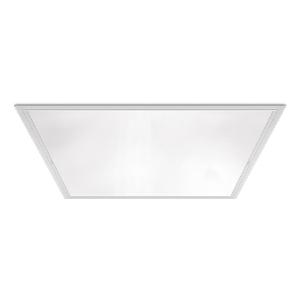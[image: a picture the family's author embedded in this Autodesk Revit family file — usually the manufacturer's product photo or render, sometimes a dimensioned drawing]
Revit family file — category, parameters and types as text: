
# Revit family: 3f_filippi_-_l_340_luce_diffusa_lgs_ip65v_3f_filippi_-_23979_-_l_340_38w-840_dali_lgs_ip65v_596x596
name_source: partatom
category: Lighting Fixtures
units: mm (PartAtom-declared; Revit-internal decimal feet)

## family parameters
Cut with Voids When Loaded = No
Host = Face
Light Source = No
Part Type = Normal
Room Calculation Point = No
Round Connector Dimension = Use Diameter
Shared = No

## types (1)
- 3F Filippi - L 340 Luce Diffusa LGS IP65V (1 x LED, 5677 lm, 43 W, 4000 K)
    Apparent Load = 43 VA
    Approval mark = ENEC
    CIE Flux Codes = 67 92 98 100 100
    Color Rendering = 80
    Color Temperature = 4000 K
    Control Gear = Electronic transformer
    Default Elevation = 1800 mm
    Description = ILLUMINOTECHNICAL
Luminous efficiency 100% (DLOR 100%, ULOR 0%).
Initial luminous flux of the luminaire 5677 lm.
Direct symmetric distribution.
Installation Interdistance Transv.D = 1.19 x hu - Long.D = 1.17 x hu.
Average luminance <3000 cd/m² for radial angles >65°.
Tabular UGR (CIE 117 - 4H-8H; S=0.25H; 70/50/20): RUG 17.8 - 17.8.
Beam angle: 87° - 86°.
Luminous efficacy 132 lm/W.
Lifetime (L93/B10): 30000 h. (tq+25°C)
Lifetime (L90/B10): 50000 h. (tq+25°C)
Lifetime (L85/B10): 80000 h. (tq+25°C)
Lifetime (L80/B10): 100000 h. (tq+25°C)
Sudden decreased luminous flux after 50000 hours: 0% (C0).
Photobiological safety in compliance with IEC/TR 62778: RG0 risk exempt, (IEC 62471).
In compliance with IEC/EN 62722-2-1 - IEC/EN 62717 standards.

SOURCE
Squared LED module 38W/840.
Energy efficiency class (UE 2019/2020 - UE 2019/2015): C.
CIE 13.3 Colour rendering index: CRI >80 (R9 <50%).
IES TM-30 Fidelity Index: Rf = 84 Rg = 95.
CCT nominal colour temperature 4000 K.
Colour initial tolerance (MacAdam): SDCM 3.

MECHANICAL
Housing in hot-galvanised steel, painted in white polyester.
Perimetral frame in white polycarbonate.
LGS micro-prismatic flat diffuser in transparent methacrylate (PMMA), multi-lenticular exterior, anti-glare.
Anti-glare opal polycarbonate filter for brightness uniformity.
Luminaire with limited surface temperature. - D - (EN 60598-2-24)
Dimensions: 596x596 mm, height 80 mm. Weight 4.45 kg.
IP65 protection degree for exposed part, IP40 for recessed part.
Mechanical strength to impacts IK06 (1 joule).
Glow-wire test resistance 650°C.

ELECTRICAL
Wiring on a separate unit.
Halogen Free DALI-2 DATI (Parts 251, 252, 253), PUSH-DIM, electronic wiring 230V-50/60Hz, power factor 0.95 at full load, THD <25%, constant output current, SELV, class II, 1 driver, 1 DALI addresse.
Power of the luminaire 43 W.
CE - IEC 60598-1 - EN 60598-1.
SAFE FLICKER: PstLM=<1 and SVM=<0.4 (IEC TR 61547-1 and IEC TR 63158), to ensure a more comfortable and safe light.
Luminaire compliant with EN 60598-2-22 for power supply from a centralised emergency system CPSS (Central Power Supply System), not incorporated in the luminaire - high risk areas excluded. The default power and flux are 100% in AC and 15% in DC.
Ambient temperature from 0°C to +40°C.
Temperature class T6 max 85°C.
Relative humidity UR: <85%.

INSTALLATION
Lay-on or pull-up recessed fitting using frame accessory.
All accessories dedicated to this product are available on the Catalog and on our website www.3F-Filippi.com.

APPLICATIONS
Suitable product for food production plants (HACCP), IFS (Food Version 6), BRC (GSFS Food Version 7).
In environments requiring protection and simplified cleaning.
Hospitals, pharmaceutical, chemical, aseptic laboratories, sterilised rooms.
Environments: with VDTs, meeting rooms, offices.
Environments: architectural, commercial, staterooms, banks.
Environments where demanding visual tasks are performed and soft diffuse light is required for optimal visual comfort and total shielding of the light source.

LIGHT MANAGEMENT
Recommended minimum setting: 10%.
The luminaire, equipped with (DALI-2 DATI) driver, can be controlled manually with 3F Easy Dim technology or automatically/manually with wired or wireless DALI/D2D control systems.
The D2D driver guarantees interoperability with other devices with the same certification by making the following information available:
Device Data (Part 251), Energy Report (Part 252), Diagnosis & Maintenance (Part 253).
In electrical systems without a regulation system (manual or automatic) and DALI bus, a suitable jumper must be made on the DA-DA terminals of the appliance.

WARNING
Luminaire designed for disposal/recycling at end-of-life.
Replaceable (LED only) light source by a professional. Replaceable control gear by a professional.
    Height = 0 mm  [stored 0 ft]
    Lamp = 1 x LED
    Lamp Light Flux = 5677 lm
    Lamp Power = 43 W
    Lamp count = 1
    Length = 596 mm
    Lifetime = 50000 h
    Luminous efficacy = 132 lm/W
    Manufacturer = 3F Filippi
    ModVariant = No
    Model = 3F Filippi - 23979 - L 340 38W-840 DALI LGS IP65V 596x596
    Mounting Place = Ceiling
    Mounting Type = Recessed
    Number of Poles = 1
    OnlyDefault = Yes
    Power Factor = 1
    Product Name = 3F Filippi - L 340 Luce Diffusa LGS IP65V
    Product group = recessed luminaire
    ProductGroupID = 4
    Protection Class = Protection class II
    Protection Degree = IP 40
    RLX_Detail_Level = 1
    RLX_Emergency_Light_Flux = 0 lm
    RLX_Emergency_Type = 0
    RLX_Emergency_Type_DB = No
    RlxData = <blob elided: 156245 chars, md5=b407dcc3>
    Socket = socket
    Standby Power = 0 W
    System Light Flux = 5677 lm
    System Power = 43 W
    Type Comments = Product without accessories
    Type Image = 3ffilippi_l_340_luce_diffusa_lgs_ip65v.jpg
    URL = http://relux.com
    VarID = ---
    Voltage = 0 V
    Weight = 0.00 kg
    Width = 596 mm

note: [stored X ft] marks values corroborated as IEEE doubles in the binary element streams (Revit-internal decimal feet)

## geometry (parser evidence)
native form markers: Blend x4, Sweep x10
no freeform markers — native parametric forms only
